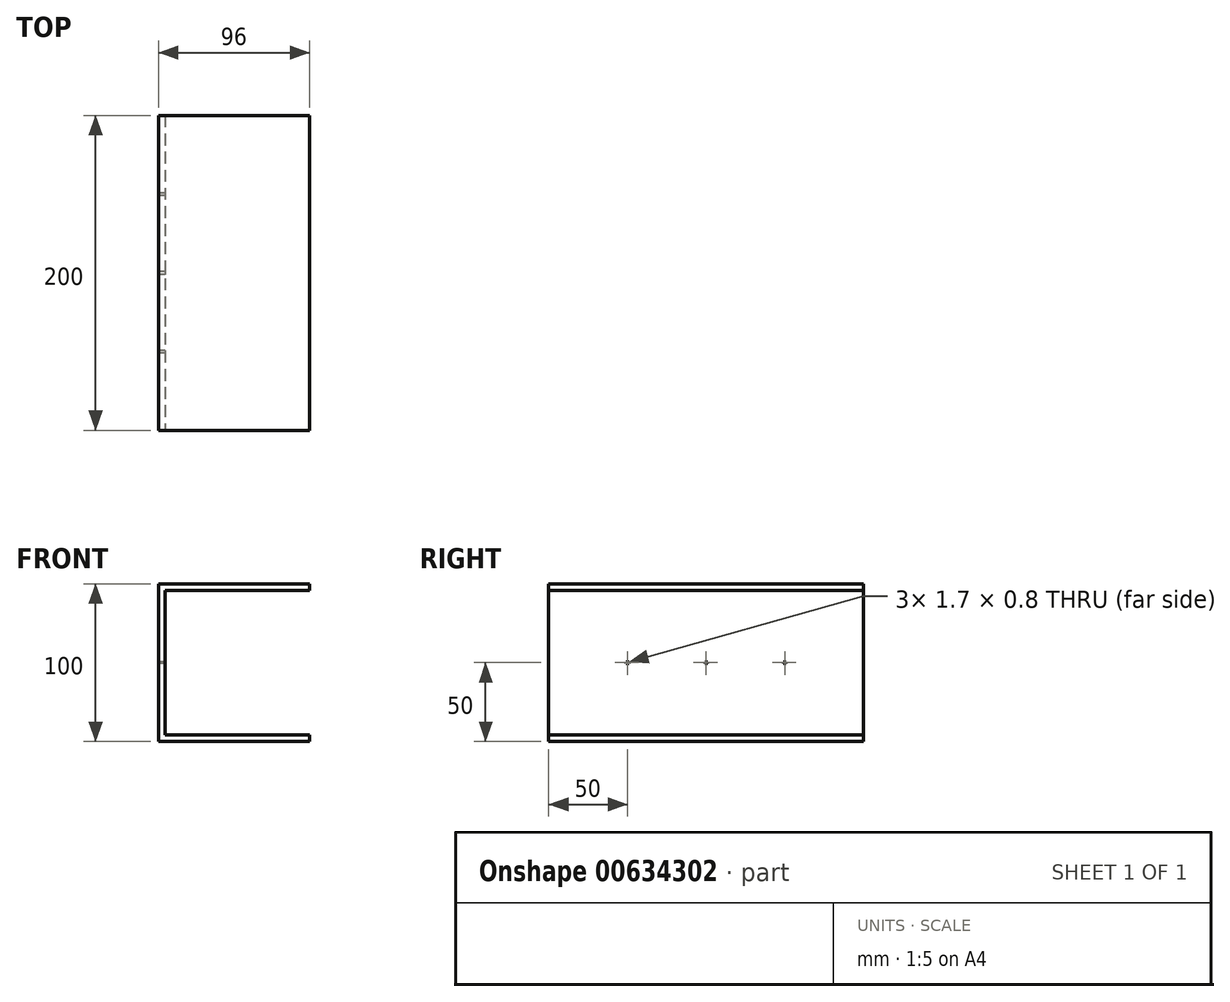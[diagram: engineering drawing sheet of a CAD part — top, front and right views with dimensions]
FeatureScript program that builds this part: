
annotation { "Feature Type Name" : "Feature", "Feature Type Description" : "" }
export const myFeature = defineFeature(function(context is Context, id is Id, definition is map)
    precondition{}
    {
        {
            var Q0;
            Q0=qCreatedBy(makeId("Front.planeOp"),FACE);
            var sketch = newSketch(context, id + "F0", { "sketchPlane" : qUnion([Q0])});
            skLineSegment(sketch, "E0.bottom", {"start": v(0, 0) * mm, "end": v(100, 0) * mm});
            skLineSegment(sketch, "E0.top", {"start": v(0, 100) * mm, "end": v(100, 100) * mm});
            skLineSegment(sketch, "E0.left", {"start": v(0, 0) * mm, "end": v(0, 100) * mm});
            skLineSegment(sketch, "E0.right", {"start": v(100, 0) * mm, "end": v(100, 100) * mm});
            skSolve(sketch);
        }
        {
            var Q0;
            Q0=qSketchRegion(id+"F0",true);
            extrude(context, id + "F1", {"entities" : qUnion([Q0]), "oppositeDirection" : true, "depth" : 200 * mm, "offsetDistance" : 25.4 * mm});
        }
        {
            var Q0;
            Q0=makeQuery(id+"F1.opExtrude","CAP_FACE",FACE,{"disambiguationData":[OSD([sQuery(id+"F0.wireOp",EDGE,"E0.bottom"),sQuery(id+"F0.wireOp",EDGE,"E0.top"),sQuery(id+"F0.wireOp",EDGE,"E0.left"),sQuery(id+"F0.wireOp",EDGE,"E0.right")])],"isStart":true});
            var sketch = newSketch(context, id + "F2", { "sketchPlane" : qUnion([Q0])});
            skLineSegment(sketch, "E1", {"start": v(0, 0) * mm, "end": v(0, 4) * mm});
            skLineSegment(sketch, "E2", {"start": v(0, 4) * mm, "end": v(4, 4) * mm});
            skLineSegment(sketch, "E3.bottom", {"start": v(4, 4) * mm, "end": v(96, 4) * mm});
            skLineSegment(sketch, "E3.top", {"start": v(4, 96) * mm, "end": v(96, 96) * mm});
            skLineSegment(sketch, "E3.left", {"start": v(4, 4) * mm, "end": v(4, 96) * mm});
            skLineSegment(sketch, "E3.right", {"start": v(96, 4) * mm, "end": v(96, 96) * mm});
            skSolve(sketch);
        }
        {
            var Q0;
            Q0=makeQuery(id+"F2.imprint","IMPRINT",FACE,{"disambiguationData":[TD([[makeQuery(id+"F2.imprint","IMPRINT",EDGE,{"derivedFrom":sQuery(id+"F2.wireOp",EDGE,"E3.bottom")}),1.0]])]});
            extrude(context, id + "F3", {"entities" : qUnion([Q0]), "operationType" : NewBodyOperationType.REMOVE, "oppositeDirection" : true, "depth" : 200 * mm, "offsetDistance" : 25.4 * mm});
        }
        {
            var Q0;
            Q0=makeQuery(id+"F1.opExtrude","SWEPT_FACE",FACE,{"disambiguationData":[OSD([sQuery(id+"F0.wireOp",EDGE,"E0.right")])]});
            var sketch = newSketch(context, id + "F4", { "sketchPlane" : qUnion([Q0])});
            skCircle(sketch, "E4", {"center": v(50, 50) * mm, "radius": 5 * mm});
            skCircle(sketch, "E5", {"center": v(100, 50) * mm, "radius": 5 * mm});
            skCircle(sketch, "E6", {"center": v(150, 50) * mm, "radius": 5 * mm});
            skCircle(sketch, "E7", {"center": v(50, 50) * mm, "radius": 7 * mm});
            skCircle(sketch, "E8", {"center": v(100, 50) * mm, "radius": 7 * mm});
            skCircle(sketch, "E9", {"center": v(150, 50) * mm, "radius": 7 * mm});
            skSolve(sketch);
        }
        {
            var Q0;
            Q0=makeQuery(id+"F4.imprint","IMPRINT",FACE,{"disambiguationData":[TD([[makeQuery(id+"F4.imprint","IMPRINT",EDGE,{"derivedFrom":sQuery(id+"F4.wireOp",EDGE,"E4")}),1.0]])]});
            var Q1;
            Q1=makeQuery(id+"F4.imprint","IMPRINT",FACE,{"disambiguationData":[TD([[makeQuery(id+"F4.imprint","IMPRINT",EDGE,{"derivedFrom":sQuery(id+"F4.wireOp",EDGE,"E5")}),1.0]])]});
            var Q2;
            Q2=makeQuery(id+"F4.imprint","IMPRINT",FACE,{"disambiguationData":[TD([[makeQuery(id+"F4.imprint","IMPRINT",EDGE,{"derivedFrom":sQuery(id+"F4.wireOp",EDGE,"E6")}),1.0]])]});
            extrude(context, id + "F5", {"entities" : qUnion([Q0, Q1, Q2]), "operationType" : NewBodyOperationType.REMOVE, "oppositeDirection" : true, "depth" : 4 * mm, "offsetDistance" : 25.4 * mm});
        }
        {
            var Q0;
            Q0=makeQuery(id+"F1.opExtrude","SWEPT_FACE",FACE,{"disambiguationData":[OSD([sQuery(id+"F0.wireOp",EDGE,"E0.left")])]});
            var sketch = newSketch(context, id + "F6", { "sketchPlane" : qUnion([Q0])});
            skLineSegment(sketch, "E10", {"start": v(-200, 0) * mm, "end": v(-150, 0) * mm});
            skLineSegment(sketch, "E11", {"start": v(-150, 0) * mm, "end": v(-100, 0) * mm});
            skLineSegment(sketch, "E12", {"start": v(-100, 0) * mm, "end": v(-50, 0) * mm});
            skLineSegment(sketch, "E13", {"start": v(-50, 0) * mm, "end": v(0, 0) * mm});
            skLineSegment(sketch, "E14", {"start": v(-150, 50) * mm, "end": v(-150, 50.4) * mm});
            skLineSegment(sketch, "E15", {"start": v(-100, 50) * mm, "end": v(-100, 58.59) * mm});
            skLineSegment(sketch, "E16", {"start": v(-50, 50) * mm, "end": v(-50, 58.59) * mm});
            skPoint(sketch, "E17", {"position": v(-150, 50) * mm});
            skLineSegment(sketch, "E18", {"start": v(-150, 0) * mm, "end": v(-150, 50) * mm});
            skLineSegment(sketch, "E19", {"start": v(-150, 50) * mm, "end": v(-150, 49.6) * mm});
            skLineSegment(sketch, "E20.bottom", {"start": v(-150.85, 50.4) * mm, "end": v(-149.15, 50.4) * mm});
            skLineSegment(sketch, "E20.top", {"start": v(-150.85, 49.6) * mm, "end": v(-149.15, 49.6) * mm});
            skLineSegment(sketch, "E20.left", {"start": v(-150.85, 50.4) * mm, "end": v(-150.85, 49.6) * mm});
            skLineSegment(sketch, "E20.right", {"start": v(-149.15, 50.4) * mm, "end": v(-149.15, 49.6) * mm});
            skLineSegment(sketch, "E21.1.0.0", {"start": v(-100.85, 50.4) * mm, "end": v(-99.15, 50.4) * mm});
            skLineSegment(sketch, "E21.1.0.1", {"start": v(-100.85, 50.4) * mm, "end": v(-100.85, 49.6) * mm});
            skLineSegment(sketch, "E21.1.0.2", {"start": v(-100.85, 49.6) * mm, "end": v(-99.15, 49.6) * mm});
            skLineSegment(sketch, "E21.1.0.3", {"start": v(-99.15, 50.4) * mm, "end": v(-99.15, 49.6) * mm});
            skLineSegment(sketch, "E21.2.0.0", {"start": v(-50.85, 50.4) * mm, "end": v(-49.15, 50.4) * mm});
            skLineSegment(sketch, "E21.2.0.1", {"start": v(-50.85, 50.4) * mm, "end": v(-50.85, 49.6) * mm});
            skLineSegment(sketch, "E21.2.0.2", {"start": v(-50.85, 49.6) * mm, "end": v(-49.15, 49.6) * mm});
            skLineSegment(sketch, "E21.2.0.3", {"start": v(-49.15, 50.4) * mm, "end": v(-49.15, 49.6) * mm});
            skLineSegment(sketch, "E21.direction1", {"start": v(-150.85, 49.6) * mm, "end": v(-100.85, 49.6) * mm, "construction": true});
            skSolve(sketch);
        }
        {
            var Q0;
            {var subQ0=sQuery(id+"F6.wireOp",EDGE,"E21.2.0.1");Q0=makeQuery(id+"F6.imprint","IMPRINT",FACE,{"disambiguationData":[TD([[makeQuery(id+"F6.imprint","IMPRINT",EDGE,{"derivedFrom":subQ0}),1.0]])]});}
            var Q1;
            {var subQ0=sQuery(id+"F6.wireOp",EDGE,"E21.1.0.1");Q1=makeQuery(id+"F6.imprint","IMPRINT",FACE,{"disambiguationData":[TD([[makeQuery(id+"F6.imprint","IMPRINT",EDGE,{"derivedFrom":subQ0}),1.0]])]});}
            var Q2;
            {var subQ1=sQuery(id+"F6.wireOp",EDGE,"E14");Q2=makeQuery(id+"F6.imprint","IMPRINT",FACE,{"disambiguationData":[TD([[makeQuery(id+"F6.imprint","IMPRINT",EDGE,{"derivedFrom":subQ1}),-1.0]])]});}
            var Q3;
            {var subQ4=sQuery(id+"F6.wireOp",EDGE,"E14");Q3=makeQuery(id+"F6.imprint","IMPRINT",FACE,{"disambiguationData":[TD([[makeQuery(id+"F6.imprint","IMPRINT",EDGE,{"derivedFrom":subQ4}),1.0]])]});}
            extrude(context, id + "F7", {"entities" : qUnion([Q0, Q1, Q2, Q3]), "operationType" : NewBodyOperationType.REMOVE, "oppositeDirection" : true, "depth" : 4 * mm, "offsetDistance" : 25.4 * mm});
        }
        {
            var Q0;
            Q0=makeQuery(id+"F4.imprint","IMPRINT",FACE,{"disambiguationData":[TD([[makeQuery(id+"F4.imprint","IMPRINT",EDGE,{"derivedFrom":sQuery(id+"F4.wireOp",EDGE,"E4")}),-1.0]])]});
            var Q1;
            Q1=makeQuery(id+"F4.imprint","IMPRINT",FACE,{"disambiguationData":[TD([[makeQuery(id+"F4.imprint","IMPRINT",EDGE,{"derivedFrom":sQuery(id+"F4.wireOp",EDGE,"E5")}),-1.0]])]});
            var Q2;
            Q2=makeQuery(id+"F4.imprint","IMPRINT",FACE,{"disambiguationData":[TD([[makeQuery(id+"F4.imprint","IMPRINT",EDGE,{"derivedFrom":sQuery(id+"F4.wireOp",EDGE,"E6")}),-1.0]])]});
            extrude(context, id + "F8", {"entities" : qUnion([Q0, Q1, Q2]), "operationType" : NewBodyOperationType.ADD, "depth" : 20 * mm, "offsetDistance" : 25.4 * mm});
        }
        {
            var Q0;
            Q0=makeQuery(id+"F8.opExtrude","CAP_FACE",FACE,{"disambiguationData":[OSD([sQuery(id+"F4.wireOp",EDGE,"E4"),sQuery(id+"F4.wireOp",EDGE,"E7")])],"isStart":false});
            var sketch = newSketch(context, id + "F9", { "sketchPlane" : qUnion([Q0])});
            skArc(sketch, "E22", {"start": v(47, 56.33) * mm, "mid": v(50, 43) * mm, "end": v(53, 56.33) * mm});
            skLineSegment(sketch, "E23", {"start": v(53, 56.33) * mm, "end": v(53, 56.33) * mm});
            skArc(sketch, "E24", {"start": v(47, 54) * mm, "mid": v(50, 45) * mm, "end": v(53, 54) * mm});
            skLineSegment(sketch, "E25", {"start": v(47, 54) * mm, "end": v(47, 56.33) * mm});
            skLineSegment(sketch, "E26", {"start": v(53, 54) * mm, "end": v(53, 56.32) * mm});
            skLineSegment(sketch, "E27.1.0.0", {"start": v(103, 54) * mm, "end": v(103, 56.32) * mm});
            skArc(sketch, "E27.1.0.1", {"start": v(97, 56.33) * mm, "mid": v(100, 43) * mm, "end": v(103, 56.33) * mm});
            skArc(sketch, "E27.1.0.2", {"start": v(97, 54) * mm, "mid": v(100, 45) * mm, "end": v(103, 54) * mm});
            skLineSegment(sketch, "E27.1.0.3", {"start": v(97, 54) * mm, "end": v(97, 56.33) * mm});
            skLineSegment(sketch, "E27.2.0.0", {"start": v(153, 54) * mm, "end": v(153, 56.32) * mm});
            skArc(sketch, "E27.2.0.1", {"start": v(147, 56.33) * mm, "mid": v(150, 43) * mm, "end": v(153, 56.33) * mm});
            skArc(sketch, "E27.2.0.2", {"start": v(147, 54) * mm, "mid": v(150, 45) * mm, "end": v(153, 54) * mm});
            skLineSegment(sketch, "E27.2.0.3", {"start": v(147, 54) * mm, "end": v(147, 56.33) * mm});
            skLineSegment(sketch, "E27.direction1", {"start": v(50, 50) * mm, "end": v(100, 50) * mm, "construction": true});
            skSolve(sketch);
        }
        {
            var Q0;
            Q0=makeQuery(id+"F3.boolean.opBoolean","COPY",FACE,{"derivedFrom":makeQuery(id+"F3.opExtrude","SWEPT_FACE",FACE,{"disambiguationData":[OSD([sQuery(id+"F2.wireOp",EDGE,"E3.right")])]})});
            var sketch = newSketch(context, id + "F10", { "sketchPlane" : qUnion([Q0])});
            skLineSegment(sketch, "E28", {"start": v(-50, 49.17) * mm, "end": v(-54.93, 49.17) * mm});
            skLineSegment(sketch, "E29", {"start": v(-50, 49.17) * mm, "end": v(-45.07, 49.17) * mm});
            skArc(sketch, "E30", {"start": v(-54.93, 49.17) * mm, "mid": v(-50, 45) * mm, "end": v(-45.07, 49.17) * mm});
            skLineSegment(sketch, "E31.1.0.0", {"start": v(-100, 49.17) * mm, "end": v(-95.07, 49.17) * mm});
            skLineSegment(sketch, "E31.1.0.1", {"start": v(-100, 49.17) * mm, "end": v(-104.93, 49.17) * mm});
            skArc(sketch, "E31.1.0.2", {"start": v(-104.93, 49.17) * mm, "mid": v(-100, 45) * mm, "end": v(-95.07, 49.17) * mm});
            skLineSegment(sketch, "E31.2.0.0", {"start": v(-150, 49.17) * mm, "end": v(-145.07, 49.17) * mm});
            skLineSegment(sketch, "E31.2.0.1", {"start": v(-150, 49.17) * mm, "end": v(-154.93, 49.17) * mm});
            skArc(sketch, "E31.2.0.2", {"start": v(-154.93, 49.17) * mm, "mid": v(-150, 45) * mm, "end": v(-145.07, 49.17) * mm});
            skLineSegment(sketch, "E31.direction1", {"start": v(-54.93, 49.17) * mm, "end": v(-104.93, 49.17) * mm, "construction": true});
            skLineSegment(sketch, "E32", {"start": v(-54.93, 49.17) * mm, "end": v(-45.07, 49.17) * mm});
            skSolve(sketch);
        }
        {
            var Q0;
            Q0=qSketchRegion(id+"F10",true);
            extrude(context, id + "F11", {"entities" : qUnion([Q0]), "operationType" : NewBodyOperationType.ADD, "oppositeDirection" : true, "depth" : 1 * mm, "offsetDistance" : 25.4 * mm});
        }
        {
            var Q0;
            Q0=makeQuery(id+"F9.imprint","IMPRINT",FACE,{"disambiguationData":[TD([[makeQuery(id+"F9.imprint","IMPRINT",EDGE,{"derivedFrom":sQuery(id+"F9.wireOp",EDGE,"E24")}),-1.0]])]});
            var Q1;
            {var subQ0=sQuery(id+"F9.wireOp",EDGE,"E27.1.0.0");Q1=makeQuery(id+"F9.imprint","IMPRINT",FACE,{"disambiguationData":[TD([[makeQuery(id+"F9.imprint","IMPRINT",EDGE,{"derivedFrom":subQ0}),-1.0]])]});}
            var Q2;
            {var subQ0=sQuery(id+"F9.wireOp",EDGE,"E27.2.0.0");Q2=makeQuery(id+"F9.imprint","IMPRINT",FACE,{"disambiguationData":[TD([[makeQuery(id+"F9.imprint","IMPRINT",EDGE,{"derivedFrom":subQ0}),-1.0]])]});}
            extrude(context, id + "F12", {"entities" : qUnion([Q0, Q1, Q2]), "operationType" : NewBodyOperationType.ADD, "depth" : 20 * mm, "offsetDistance" : 25.4 * mm});
        }
        {
            var Q0;
            Q0=makeQuery(id+"F11.boolean.opBoolean","MERGE",FACE,{"derivedFrom":[makeQuery(id+"F3.boolean.opBoolean","COPY",FACE,{"derivedFrom":makeQuery(id+"F3.opExtrude","SWEPT_FACE",FACE,{"disambiguationData":[OSD([sQuery(id+"F2.wireOp",EDGE,"E3.right")])]})}),makeQuery(id+"F11.opExtrude","CAP_FACE",FACE,{"disambiguationData":[OSD([sQuery(id+"F10.wireOp",EDGE,"E30"),sQuery(id+"F10.wireOp",EDGE,"E32")])],"isStart":true}),makeQuery(id+"F11.opExtrude","CAP_FACE",FACE,{"disambiguationData":[OSD([sQuery(id+"F10.wireOp",EDGE,"E31.1.0.0"),sQuery(id+"F10.wireOp",EDGE,"E31.1.0.1"),sQuery(id+"F10.wireOp",EDGE,"E31.1.0.2")])],"isStart":true}),makeQuery(id+"F11.opExtrude","CAP_FACE",FACE,{"disambiguationData":[OSD([sQuery(id+"F10.wireOp",EDGE,"E31.2.0.0"),sQuery(id+"F10.wireOp",EDGE,"E31.2.0.1"),sQuery(id+"F10.wireOp",EDGE,"E31.2.0.2")])],"isStart":true})]});
            var sketch = newSketch(context, id + "F13", { "sketchPlane" : qUnion([Q0])});
            skLineSegment(sketch, "E33.bottom", {"start": v(-207.4, 108.81) * mm, "end": v(8.82, 108.81) * mm});
            skLineSegment(sketch, "E33.top", {"start": v(-207.4, -15.6) * mm, "end": v(8.82, -15.6) * mm});
            skLineSegment(sketch, "E33.left", {"start": v(-207.4, 108.81) * mm, "end": v(-207.4, -15.6) * mm});
            skLineSegment(sketch, "E33.right", {"start": v(8.82, 108.81) * mm, "end": v(8.82, -15.6) * mm});
            skSolve(sketch);
        }
        {
            var Q0;
            Q0 = qSketchRegion(id + "F13", true);
            extrude(context, id + "F14", {"entities" : qUnion([Q0]), "operationType" : NewBodyOperationType.REMOVE, "oppositeDirection" : true, "depth" : 304.8 * mm, "offsetDistance" : 25.4 * mm});
        }
    });
